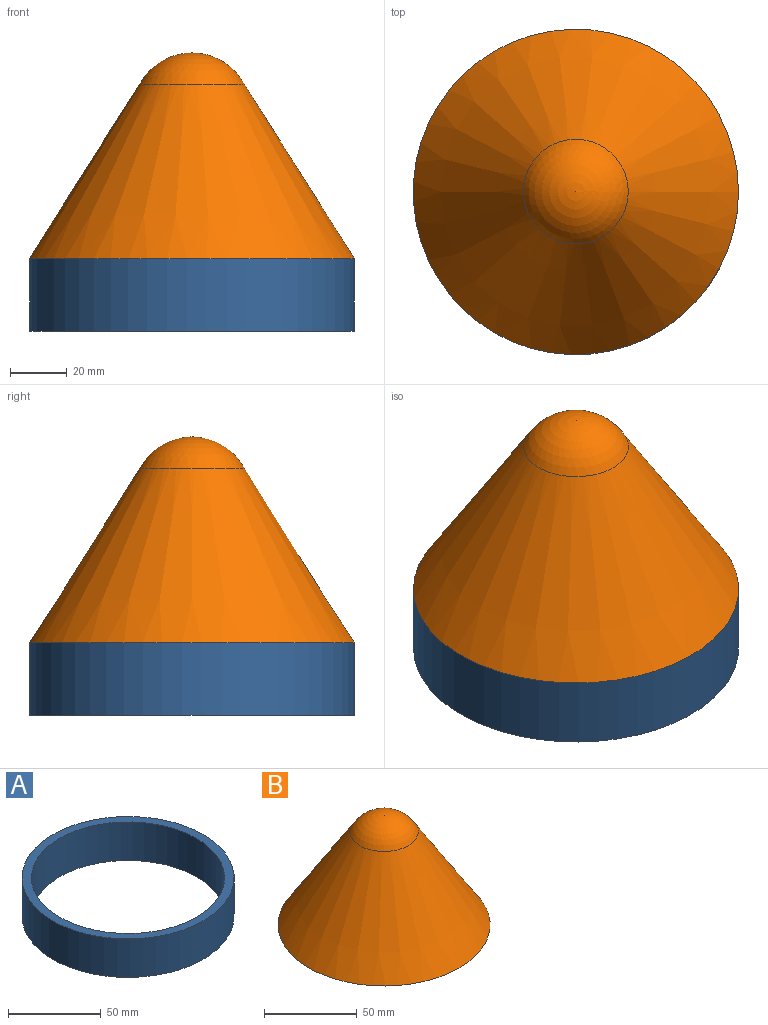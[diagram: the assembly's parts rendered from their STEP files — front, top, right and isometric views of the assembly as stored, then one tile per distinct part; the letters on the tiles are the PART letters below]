
ASSEMBLY  parts=2 mates=1
PART A: 4 faces, bbox 114.3x114.3x25.4 mm
  f0: cylinder r=57.15mm len=114.3mm, axis (0,0,-1), area 9120.7mm2, adj f1,f2
  f1: plane 114.3x114.3mm, normal (0,0,1), area 1743.1mm2, adj f0,f3
  f2: plane 114.3x114.3mm, normal (0,0,-1), area 1743.1mm2, adj f0,f3
  f3: cylinder r=52.07mm len=104.14mm, axis (0,0,1), area 8310mm2, adj f1,f2
PART B: 5 faces, bbox 114.3x114.3x72.4 mm
  f0: cone r=57.15mm half-angle=32.3deg, axis (0,0,-1), area 17232.2mm2, adj f1,f2
  f1: sphere r=20.93mm, area 1442.2mm2, adj f0
  f2: plane 114.3x114.3mm, normal (0,0,-1), area 2043.7mm2, adj f0,f3
  f3: cone r=52.85mm half-angle=32.3deg, axis (0,0,-1), area 14241.3mm2, adj f2,f4
  f4: sphere r=15.85mm, area 840.9mm2, adj f3
PLACE A t=(28.03,-52.07,-75.43)mm
PLACE B t=(28.03,-52.07,21.03)mm
MATE fastened A.f0 <-> B.f0  axis (0,0,1) through (28.03,-52.07,-50.03)mm
